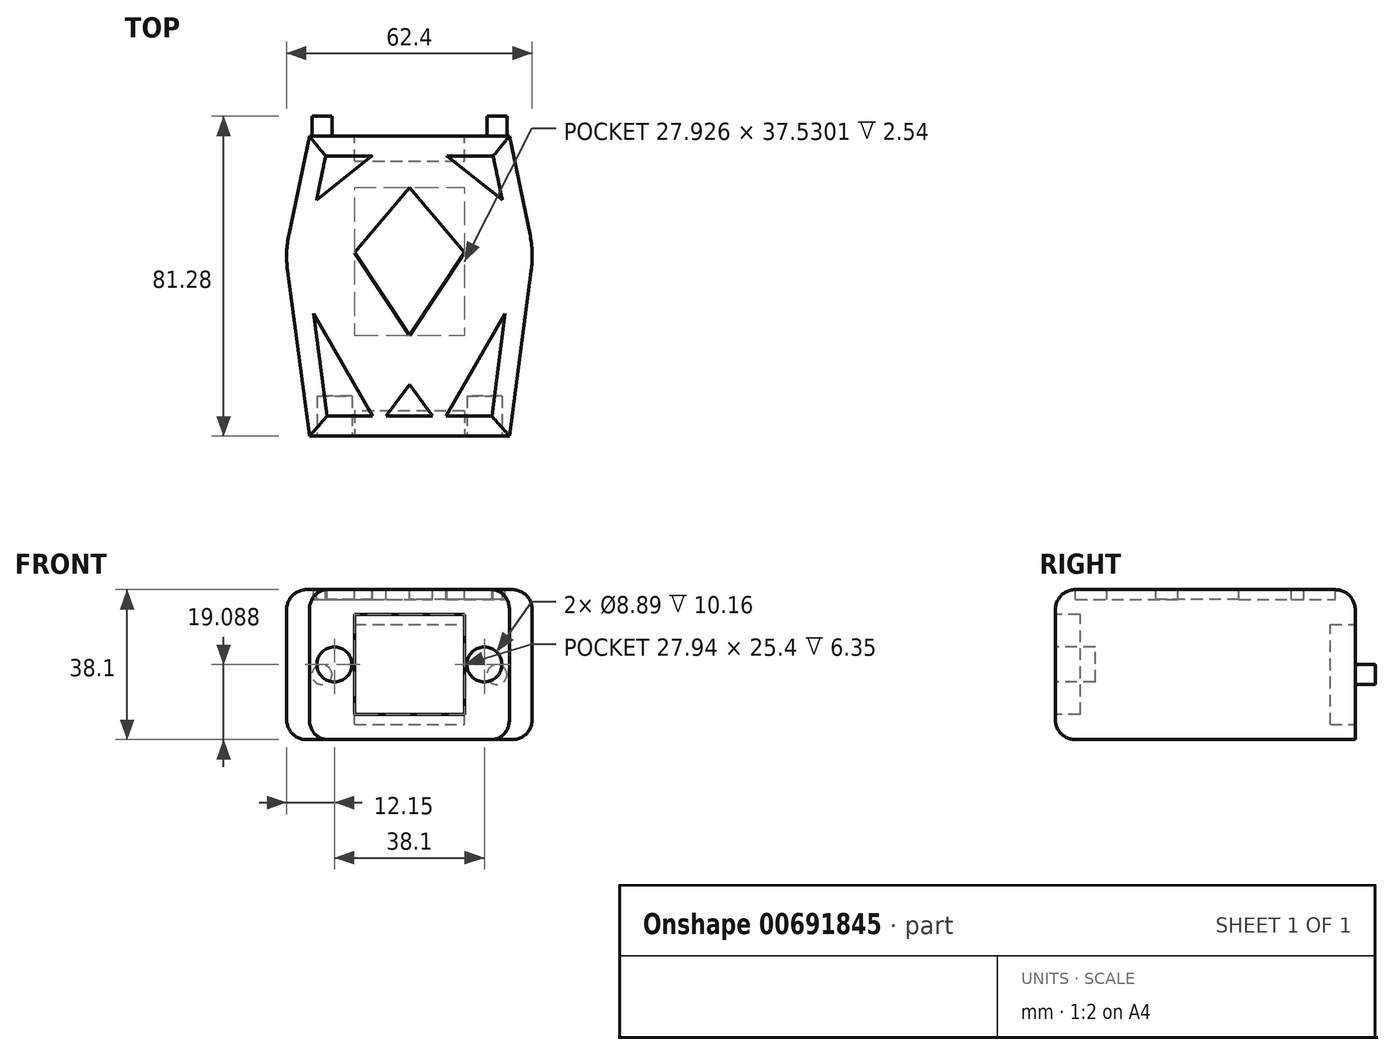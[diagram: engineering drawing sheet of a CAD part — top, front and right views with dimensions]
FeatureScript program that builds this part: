
annotation { "Feature Type Name" : "Feature", "Feature Type Description" : "" }
export const myFeature = defineFeature(function(context is Context, id is Id, definition is map)
    precondition{}
    {
        {
            var Q0;
            Q0=qCreatedBy(makeId("Top.planeOp"),FACE);
            var sketch = newSketch(context, id + "F0", { "sketchPlane" : qUnion([Q0])});
            skPoint(sketch, "E0", {"position": v(-25.4, 29.5) * mm});
            skPoint(sketch, "E1", {"position": v(-31.58, 0) * mm});
            skPoint(sketch, "E2", {"position": v(-25.4, -46.7) * mm});
            skLineSegment(sketch, "E3", {"start": v(-25.4, 29.5) * mm, "end": v(-31.58, 0) * mm});
            skLineSegment(sketch, "E4", {"start": v(-31.58, 0) * mm, "end": v(-25.4, -46.7) * mm});
            skPoint(sketch, "E5.MirrorP", {"position": v(31.58, 0) * mm});
            skLineSegment(sketch, "E6.MirrorCS", {"start": v(31.58, 0) * mm, "end": v(25.4, -46.7) * mm});
            skPoint(sketch, "E7.MirrorP", {"position": v(25.4, 29.5) * mm});
            skLineSegment(sketch, "E8.MirrorCS", {"start": v(25.4, 29.5) * mm, "end": v(31.58, 0) * mm});
            skLineSegment(sketch, "E9", {"start": v(-25.4, 29.5) * mm, "end": v(25.4, 29.5) * mm});
            skLineSegment(sketch, "E10", {"start": v(25.4, -46.7) * mm, "end": v(-25.4, -46.7) * mm});
            skSolve(sketch);
        }
        {
            var Q0;
            Q0=qSketchRegion(id+"F0",true);
            extrude(context, id + "F1", {"entities" : qUnion([Q0]), "depth" : 38.1 * mm, "offsetDistance" : 25.4 * mm});
        }
        {
            var Q0;
            Q0=makeQuery(id+"F1.opExtrude","SWEPT_EDGE",EDGE,{"disambiguationData":[OSD([sQuery(id+"F0.wireOp",EDGE,"E6.MirrorCS"),sQuery(id+"F0.wireOp",EDGE,"E8.MirrorCS")])]});
            fillet(context, id + "F2", {"entities" : qUnion([Q0]), "radius" : 27.94 * mm, "tangentPropagation" : true, "allowEdgeOverflow" : false});
        }
        {
            var Q0;
            Q0=makeQuery(id+"F1.opExtrude","SWEPT_EDGE",EDGE,{"disambiguationData":[OSD([sQuery(id+"F0.wireOp",EDGE,"E3"),sQuery(id+"F0.wireOp",EDGE,"E4")])]});
            fillet(context, id + "F3", {"entities" : qUnion([Q0]), "radius" : 27.94 * mm, "tangentPropagation" : true, "allowEdgeOverflow" : false});
        }
        {
            var Q0;
            Q0=makeQuery(id+"F1.opExtrude","CAP_EDGE",EDGE,{"disambiguationData":[OSD([sQuery(id+"F0.wireOp",EDGE,"E10")])],"isStart":true});
            var Q1;
            Q1=makeQuery(id+"F1.opExtrude","CAP_EDGE",EDGE,{"disambiguationData":[OSD([sQuery(id+"F0.wireOp",EDGE,"E4")])],"isStart":true});
            var Q2;
            {var subQ0=sQuery(id+"F0.wireOp",EDGE,"E9");var subQ1=sQuery(id+"F0.wireOp",EDGE,"E3");Q2=makeQuery(id+"FuhFUaFevBtmED8_1.opFillet","BLEND_EDGE",EDGE,{"blendedFrom":[makeQuery(id+"F1.opExtrude","SWEPT_EDGE",EDGE,{"disambiguationData":[OSD([subQ1,subQ0])]}),makeQuery(id+"F1.opExtrude","CAP_FACE",FACE,{"disambiguationData":[OSD([subQ1,sQuery(id+"F0.wireOp",EDGE,"E4"),sQuery(id+"F0.wireOp",EDGE,"E6.MirrorCS"),sQuery(id+"F0.wireOp",EDGE,"E8.MirrorCS"),subQ0,sQuery(id+"F0.wireOp",EDGE,"E10")])],"isStart":true})],"blendedInto":[makeQuery(id+"F1.opExtrude","CAP_FACE",FACE,{"disambiguationData":[OSD([subQ1,sQuery(id+"F0.wireOp",EDGE,"E4"),sQuery(id+"F0.wireOp",EDGE,"E6.MirrorCS"),sQuery(id+"F0.wireOp",EDGE,"E8.MirrorCS"),subQ0,sQuery(id+"F0.wireOp",EDGE,"E10")])],"isStart":true})]});}
            var Q3;
            {var subQ0=sQuery(id+"F0.wireOp",EDGE,"E9");var subQ1=sQuery(id+"F0.wireOp",EDGE,"E8.MirrorCS");Q3=makeQuery(id+"FAzzm3Lc1GU829s_1.opFillet","BLEND_EDGE",EDGE,{"blendedFrom":[makeQuery(id+"F1.opExtrude","SWEPT_EDGE",EDGE,{"disambiguationData":[OSD([subQ1,subQ0])]}),makeQuery(id+"F1.opExtrude","CAP_FACE",FACE,{"disambiguationData":[OSD([sQuery(id+"F0.wireOp",EDGE,"E3"),sQuery(id+"F0.wireOp",EDGE,"E4"),sQuery(id+"F0.wireOp",EDGE,"E6.MirrorCS"),subQ1,subQ0,sQuery(id+"F0.wireOp",EDGE,"E10")])],"isStart":true})],"blendedInto":[makeQuery(id+"F1.opExtrude","CAP_FACE",FACE,{"disambiguationData":[OSD([sQuery(id+"F0.wireOp",EDGE,"E3"),sQuery(id+"F0.wireOp",EDGE,"E4"),sQuery(id+"F0.wireOp",EDGE,"E6.MirrorCS"),subQ1,subQ0,sQuery(id+"F0.wireOp",EDGE,"E10")])],"isStart":true})]});}
            var Q4;
            {var subQ0=sQuery(id+"F0.wireOp",EDGE,"E8.MirrorCS");var subQ1=sQuery(id+"F0.wireOp",EDGE,"E6.MirrorCS");Q4=makeQuery(id+"F2.opFillet","BLEND_EDGE",EDGE,{"blendedFrom":[makeQuery(id+"F1.opExtrude","SWEPT_EDGE",EDGE,{"disambiguationData":[OSD([subQ1,subQ0])]}),makeQuery(id+"F1.opExtrude","CAP_FACE",FACE,{"disambiguationData":[OSD([sQuery(id+"F0.wireOp",EDGE,"E3"),sQuery(id+"F0.wireOp",EDGE,"E4"),subQ1,subQ0,sQuery(id+"F0.wireOp",EDGE,"E9"),sQuery(id+"F0.wireOp",EDGE,"E10")])],"isStart":true})],"blendedInto":[makeQuery(id+"F1.opExtrude","CAP_FACE",FACE,{"disambiguationData":[OSD([sQuery(id+"F0.wireOp",EDGE,"E3"),sQuery(id+"F0.wireOp",EDGE,"E4"),subQ1,subQ0,sQuery(id+"F0.wireOp",EDGE,"E9"),sQuery(id+"F0.wireOp",EDGE,"E10")])],"isStart":true})]});}
            var Q5;
            Q5=makeQuery(id+"F1.opExtrude","CAP_EDGE",EDGE,{"disambiguationData":[OSD([sQuery(id+"F0.wireOp",EDGE,"E6.MirrorCS")])],"isStart":true});
            var Q6;
            {var subQ0=sQuery(id+"F0.wireOp",EDGE,"E4");var subQ1=sQuery(id+"F0.wireOp",EDGE,"E3");Q6=makeQuery(id+"F3.opFillet","BLEND_EDGE",EDGE,{"blendedFrom":[makeQuery(id+"F1.opExtrude","SWEPT_EDGE",EDGE,{"disambiguationData":[OSD([subQ1,subQ0])]}),makeQuery(id+"F1.opExtrude","CAP_FACE",FACE,{"disambiguationData":[OSD([subQ1,subQ0,sQuery(id+"F0.wireOp",EDGE,"E6.MirrorCS"),sQuery(id+"F0.wireOp",EDGE,"E8.MirrorCS"),sQuery(id+"F0.wireOp",EDGE,"E9"),sQuery(id+"F0.wireOp",EDGE,"E10")])],"isStart":true})],"blendedInto":[makeQuery(id+"F1.opExtrude","CAP_FACE",FACE,{"disambiguationData":[OSD([subQ1,subQ0,sQuery(id+"F0.wireOp",EDGE,"E6.MirrorCS"),sQuery(id+"F0.wireOp",EDGE,"E8.MirrorCS"),sQuery(id+"F0.wireOp",EDGE,"E9"),sQuery(id+"F0.wireOp",EDGE,"E10")])],"isStart":true})]});}
            fillet(context, id + "F4", {"entities" : qUnion([Q0, Q1, Q2, Q3, Q4, Q5, Q6]), "radius" : 5.08 * mm, "tangentPropagation" : true, "allowEdgeOverflow" : false});
        }
        {
            var Q0;
            Q0=makeQuery(id+"F1.opExtrude","CAP_EDGE",EDGE,{"disambiguationData":[OSD([sQuery(id+"F0.wireOp",EDGE,"E10")])],"isStart":false});
            var Q1;
            Q1=makeQuery(id+"F1.opExtrude","CAP_EDGE",EDGE,{"disambiguationData":[OSD([sQuery(id+"F0.wireOp",EDGE,"E4")])],"isStart":false});
            var Q2;
            {var subQ0=sQuery(id+"F0.wireOp",EDGE,"E9");var subQ1=sQuery(id+"F0.wireOp",EDGE,"E3");Q2=makeQuery(id+"FuhFUaFevBtmED8_1.opFillet","BLEND_EDGE",EDGE,{"blendedFrom":[makeQuery(id+"F1.opExtrude","SWEPT_EDGE",EDGE,{"disambiguationData":[OSD([subQ1,subQ0])]}),makeQuery(id+"F1.opExtrude","CAP_FACE",FACE,{"disambiguationData":[OSD([subQ1,sQuery(id+"F0.wireOp",EDGE,"E4"),sQuery(id+"F0.wireOp",EDGE,"E6.MirrorCS"),sQuery(id+"F0.wireOp",EDGE,"E8.MirrorCS"),subQ0,sQuery(id+"F0.wireOp",EDGE,"E10")])],"isStart":false})],"blendedInto":[makeQuery(id+"F1.opExtrude","CAP_FACE",FACE,{"disambiguationData":[OSD([subQ1,sQuery(id+"F0.wireOp",EDGE,"E4"),sQuery(id+"F0.wireOp",EDGE,"E6.MirrorCS"),sQuery(id+"F0.wireOp",EDGE,"E8.MirrorCS"),subQ0,sQuery(id+"F0.wireOp",EDGE,"E10")])],"isStart":false})]});}
            var Q3;
            Q3=makeQuery(id+"F1.opExtrude","CAP_FACE",FACE,{"disambiguationData":[OSD([sQuery(id+"F0.wireOp",EDGE,"E3"),sQuery(id+"F0.wireOp",EDGE,"E4"),sQuery(id+"F0.wireOp",EDGE,"E6.MirrorCS"),sQuery(id+"F0.wireOp",EDGE,"E8.MirrorCS"),sQuery(id+"F0.wireOp",EDGE,"E9"),sQuery(id+"F0.wireOp",EDGE,"E10")])],"isStart":false});
            fillet(context, id + "F5", {"entities" : qUnion([Q0, Q1, Q2, Q3]), "radius" : 5.08 * mm, "tangentPropagation" : true, "allowEdgeOverflow" : false});
        }
        {
            var Q0;
            Q0=makeQuery(id+"F1.opExtrude","SWEPT_FACE",FACE,{"disambiguationData":[OSD([sQuery(id+"F0.wireOp",EDGE,"E10")])]});
            cPlane(context, id + "F6", {"entities" : qUnion([Q0]), "cplaneType" : CPlaneType.OFFSET, "offset" : 0 * mm, "width" : 152.4 * mm, "height" : 152.4 * mm});
        }
        {
            var Q0;
            Q0=qCreatedBy(id+"F6.planeOp",FACE);
            var sketch = newSketch(context, id + "F7", { "sketchPlane" : qUnion([Q0])});
            skLineSegment(sketch, "E11.bottom", {"start": v(13.97, 8.3) * mm, "end": v(-13.97, 8.3) * mm});
            skLineSegment(sketch, "E11.top", {"start": v(13.97, 29.88) * mm, "end": v(-13.97, 29.88) * mm});
            skLineSegment(sketch, "E11.left", {"start": v(13.97, 8.3) * mm, "end": v(13.97, 29.88) * mm});
            skLineSegment(sketch, "E11.right", {"start": v(-13.97, 8.3) * mm, "end": v(-13.97, 29.88) * mm});
            skPoint(sketch, "E11.middle", {"position": v(0, 19.09) * mm});
            skCircle(sketch, "E12", {"center": v(19.05, 19.09) * mm, "radius": 4.45 * mm});
            skCircle(sketch, "E13", {"center": v(-19.05, 19.09) * mm, "radius": 4.45 * mm});
            skSolve(sketch);
        }
        {
            var Q0;
            Q0=makeQuery(id+"F7.imprint","IMPRINT",FACE,{"disambiguationData":[TD([[makeQuery(id+"F7.imprint","IMPRINT",EDGE,{"derivedFrom":sQuery(id+"F7.wireOp",EDGE,"E13")}),1.0]])]});
            var Q1;
            Q1=makeQuery(id+"F7.imprint","IMPRINT",FACE,{"disambiguationData":[TD([[makeQuery(id+"F7.imprint","IMPRINT",EDGE,{"derivedFrom":sQuery(id+"F7.wireOp",EDGE,"E12")}),1.0]])]});
            extrude(context, id + "F8", {"entities" : qUnion([Q0, Q1]), "operationType" : NewBodyOperationType.REMOVE, "oppositeDirection" : true, "depth" : 10.16 * mm, "offsetDistance" : 25.4 * mm});
        }
        {
            var Q0;
            Q0=qCreatedBy(id+"F6.planeOp",FACE);
            var sketch = newSketch(context, id + "F9", { "sketchPlane" : qUnion([Q0])});
            skLineSegment(sketch, "E14.bottom", {"start": v(13.97, 6.39) * mm, "end": v(-13.97, 6.39) * mm});
            skLineSegment(sketch, "E14.top", {"start": v(13.97, 31.79) * mm, "end": v(-13.97, 31.79) * mm});
            skLineSegment(sketch, "E14.left", {"start": v(13.97, 6.39) * mm, "end": v(13.97, 31.79) * mm});
            skLineSegment(sketch, "E14.right", {"start": v(-13.97, 6.39) * mm, "end": v(-13.97, 31.79) * mm});
            skPoint(sketch, "E14.middle", {"position": v(0, 19.09) * mm});
            skSolve(sketch);
        }
        {
            var Q0;
            Q0=qSketchRegion(id+"F9",true);
            extrude(context, id + "F10", {"entities" : qUnion([Q0]), "operationType" : NewBodyOperationType.REMOVE, "oppositeDirection" : true, "depth" : 6.35 * mm, "offsetDistance" : 25.4 * mm});
        }
        {
            var Q0;
            Q0=makeQuery(id+"F1.opExtrude","CAP_FACE",FACE,{"disambiguationData":[OSD([sQuery(id+"F0.wireOp",EDGE,"E3"),sQuery(id+"F0.wireOp",EDGE,"E4"),sQuery(id+"F0.wireOp",EDGE,"E6.MirrorCS"),sQuery(id+"F0.wireOp",EDGE,"E8.MirrorCS"),sQuery(id+"F0.wireOp",EDGE,"E9"),sQuery(id+"F0.wireOp",EDGE,"E10")])],"isStart":false});
            cPlane(context, id + "F11", {"entities" : qUnion([Q0]), "cplaneType" : CPlaneType.OFFSET, "offset" : 0 * mm, "width" : 152.4 * mm, "height" : 152.4 * mm});
        }
        {
            var Q0;
            Q0=makeQuery(id+"F1.opExtrude","SWEPT_FACE",FACE,{"disambiguationData":[OSD([sQuery(id+"F0.wireOp",EDGE,"E9")])]});
            var sketch = newSketch(context, id + "F12", { "sketchPlane" : qUnion([Q0])});
            skLineSegment(sketch, "E15.bottom", {"start": v(13.97, 3.8) * mm, "end": v(-13.97, 3.8) * mm});
            skLineSegment(sketch, "E15.top", {"start": v(13.97, 29.21) * mm, "end": v(-13.97, 29.21) * mm});
            skLineSegment(sketch, "E15.left", {"start": v(13.97, 3.8) * mm, "end": v(13.97, 29.21) * mm});
            skLineSegment(sketch, "E15.right", {"start": v(-13.97, 3.8) * mm, "end": v(-13.97, 29.21) * mm});
            skPoint(sketch, "E15.middle", {"position": v(0, 16.5) * mm});
            skCircle(sketch, "E16", {"center": v(-22.23, 16.5) * mm, "radius": 2.54 * mm});
            skPoint(sketch, "E16.centerSnap0", {"position": v(-13.97, 16.5) * mm});
            skPoint(sketch, "E17.centerSnap0", {"position": v(0, 29.21) * mm});
            skCircle(sketch, "E18", {"center": v(22.23, 16.51) * mm, "radius": 2.54 * mm});
            skPoint(sketch, "E19.centerSnap0", {"position": v(0, 3.8) * mm});
            skSolve(sketch);
        }
        {
            var Q0;
            Q0=makeQuery(id+"F12.imprint","IMPRINT",FACE,{"disambiguationData":[TD([[makeQuery(id+"F12.imprint","IMPRINT",EDGE,{"derivedFrom":sQuery(id+"F12.wireOp",EDGE,"E15.bottom")}),-1.0]])]});
            extrude(context, id + "F13", {"entities" : qUnion([Q0]), "operationType" : NewBodyOperationType.REMOVE, "oppositeDirection" : true, "depth" : 6.35 * mm, "offsetDistance" : 25.4 * mm});
        }
        {
            var Q0;
            Q0=makeQuery(id+"F12.imprint","IMPRINT",FACE,{"disambiguationData":[TD([[makeQuery(id+"F12.imprint","IMPRINT",EDGE,{"derivedFrom":sQuery(id+"F12.wireOp",EDGE,"E16")}),1.0]])]});
            var Q1;
            Q1=makeQuery(id+"F12.imprint","IMPRINT",FACE,{"disambiguationData":[TD([[makeQuery(id+"F12.imprint","IMPRINT",EDGE,{"derivedFrom":sQuery(id+"F12.wireOp",EDGE,"E18")}),1.0]])]});
            extrude(context, id + "F14", {"entities" : qUnion([Q0, Q1]), "operationType" : NewBodyOperationType.ADD, "depth" : 5.08 * mm, "offsetDistance" : 25.4 * mm});
        }
        {
            var Q0;
            Q0=qCreatedBy(id+"F11.planeOp",FACE);
            var sketch = newSketch(context, id + "F15", { "sketchPlane" : qUnion([Q0])});
            skPoint(sketch, "E20", {"position": v(-20.93, -41.56) * mm});
            skPoint(sketch, "E21", {"position": v(-24.34, -15.52) * mm});
            skPoint(sketch, "E22", {"position": v(-9.34, -41.56) * mm});
            skLineSegment(sketch, "E23", {"start": v(-24.34, -15.52) * mm, "end": v(-20.93, -41.56) * mm});
            skLineSegment(sketch, "E24", {"start": v(-20.93, -41.56) * mm, "end": v(-9.34, -41.56) * mm});
            skLineSegment(sketch, "E25", {"start": v(-9.34, -41.56) * mm, "end": v(-24.34, -15.52) * mm});
            skLineSegment(sketch, "E26.MirrorCS", {"start": v(9.34, -41.56) * mm, "end": v(24.34, -15.52) * mm});
            skLineSegment(sketch, "E27.MirrorCS", {"start": v(20.93, -41.56) * mm, "end": v(9.34, -41.56) * mm});
            skLineSegment(sketch, "E28.MirrorCS", {"start": v(24.34, -15.52) * mm, "end": v(20.93, -41.56) * mm});
            skPoint(sketch, "E29", {"position": v(-5.91, -41.56) * mm});
            skPoint(sketch, "E30", {"position": v(0, -33.62) * mm});
            skLineSegment(sketch, "E31", {"start": v(-5.91, -41.56) * mm, "end": v(0, -33.62) * mm});
            skLineSegment(sketch, "E32.MirrorCS", {"start": v(5.91, -41.56) * mm, "end": v(0, -33.62) * mm});
            skLineSegment(sketch, "E33", {"start": v(-5.91, -41.56) * mm, "end": v(5.91, -41.56) * mm});
            skPoint(sketch, "E34", {"position": v(-21.28, 24.44) * mm});
            skPoint(sketch, "E35", {"position": v(-9.51, 24.48) * mm});
            skPoint(sketch, "E36", {"position": v(-23.6, 13.26) * mm});
            skLineSegment(sketch, "E37", {"start": v(-23.6, 13.26) * mm, "end": v(-21.28, 24.44) * mm});
            skLineSegment(sketch, "E38", {"start": v(-23.6, 13.26) * mm, "end": v(-9.51, 24.48) * mm});
            skLineSegment(sketch, "E39", {"start": v(-21.28, 24.44) * mm, "end": v(-9.51, 24.48) * mm});
            skLineSegment(sketch, "E40.MirrorCS", {"start": v(23.6, 13.26) * mm, "end": v(9.51, 24.48) * mm});
            skLineSegment(sketch, "E41.MirrorCS", {"start": v(21.28, 24.44) * mm, "end": v(9.51, 24.48) * mm});
            skLineSegment(sketch, "E42.MirrorCS", {"start": v(23.6, 13.26) * mm, "end": v(21.28, 24.44) * mm});
            skPoint(sketch, "E43", {"position": v(-13.96, 0) * mm});
            skPoint(sketch, "E44", {"position": v(0, 16.4) * mm});
            skPoint(sketch, "E45", {"position": v(0, -21.13) * mm});
            skLineSegment(sketch, "E46", {"start": v(-13.96, 0) * mm, "end": v(0, 16.4) * mm});
            skLineSegment(sketch, "E47", {"start": v(-13.96, 0) * mm, "end": v(0, -21.13) * mm});
            skLineSegment(sketch, "E48.MirrorCS", {"start": v(13.96, 0) * mm, "end": v(0, 16.4) * mm});
            skLineSegment(sketch, "E49.MirrorCS", {"start": v(13.96, 0) * mm, "end": v(0, -21.13) * mm});
            skSolve(sketch);
        }
        {
            var Q0;
            Q0 = qSketchRegion(id + "F15", true);
            extrude(context, id + "F16", {"entities" : qUnion([Q0]), "operationType" : NewBodyOperationType.REMOVE, "oppositeDirection" : true, "depth" : 2.54 * mm, "offsetDistance" : 25.4 * mm});
        }
    });
